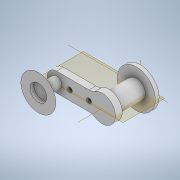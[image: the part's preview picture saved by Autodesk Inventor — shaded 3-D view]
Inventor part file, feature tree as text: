
AUTODESK INVENTOR PART (.ipt)
format: ipt  version: 2022 (Build 260153000, 153)  size: 161,280 bytes
history: native  units: mm
features: sketch x5, extrude x4, other x1, plane x1, revolve x1
ambient origin geometry x8: Origin, YZ Plane, XZ Plane, XY Plane, X Axis, Y Axis, Z Axis, Center Point
bodies: Body1 (feature_tree)
feature tree (12):
  other  "Sólido1"
  extrude  "Extrusión1"  Depth=5.0mm TaperAngle=0.0deg
  extrude  "Extrusión2"  Depth=36.0mm TaperAngle=0.0deg
  extrude  "Extrusión3"  Depth=9.0mm
  plane  "Plano de trabajo1"
  revolve  "Revolución1"  [1 undecoded]
  extrude  "Extrusión4"  Depth=5.0mm
  sketch  "Boceto2"  dims[d0=50.0mm d1=5.0mm d2=0.0mm]
  sketch  "Boceto3"  dims[d3=24.0mm d4=36.0mm d5=0.0mm]
  sketch  "Boceto4"  dims[d6=9.0mm d7=0.0mm d8=14.0mm]
  sketch  "Boceto6"  dims[d9=9.0mm d10=13.0mm]
  sketch  "Boceto7"  dims[d11=13.0mm d12=46.0mm d13=11.0mm d14=90.0deg d15=22.0mm d16=5.0mm d17=0.0mm]
note: 1 required parameter value undecoded (feature->parameter linkage not recoverable at this tier; creation-order binding heuristic only, values carry confidence <= 0.55)
